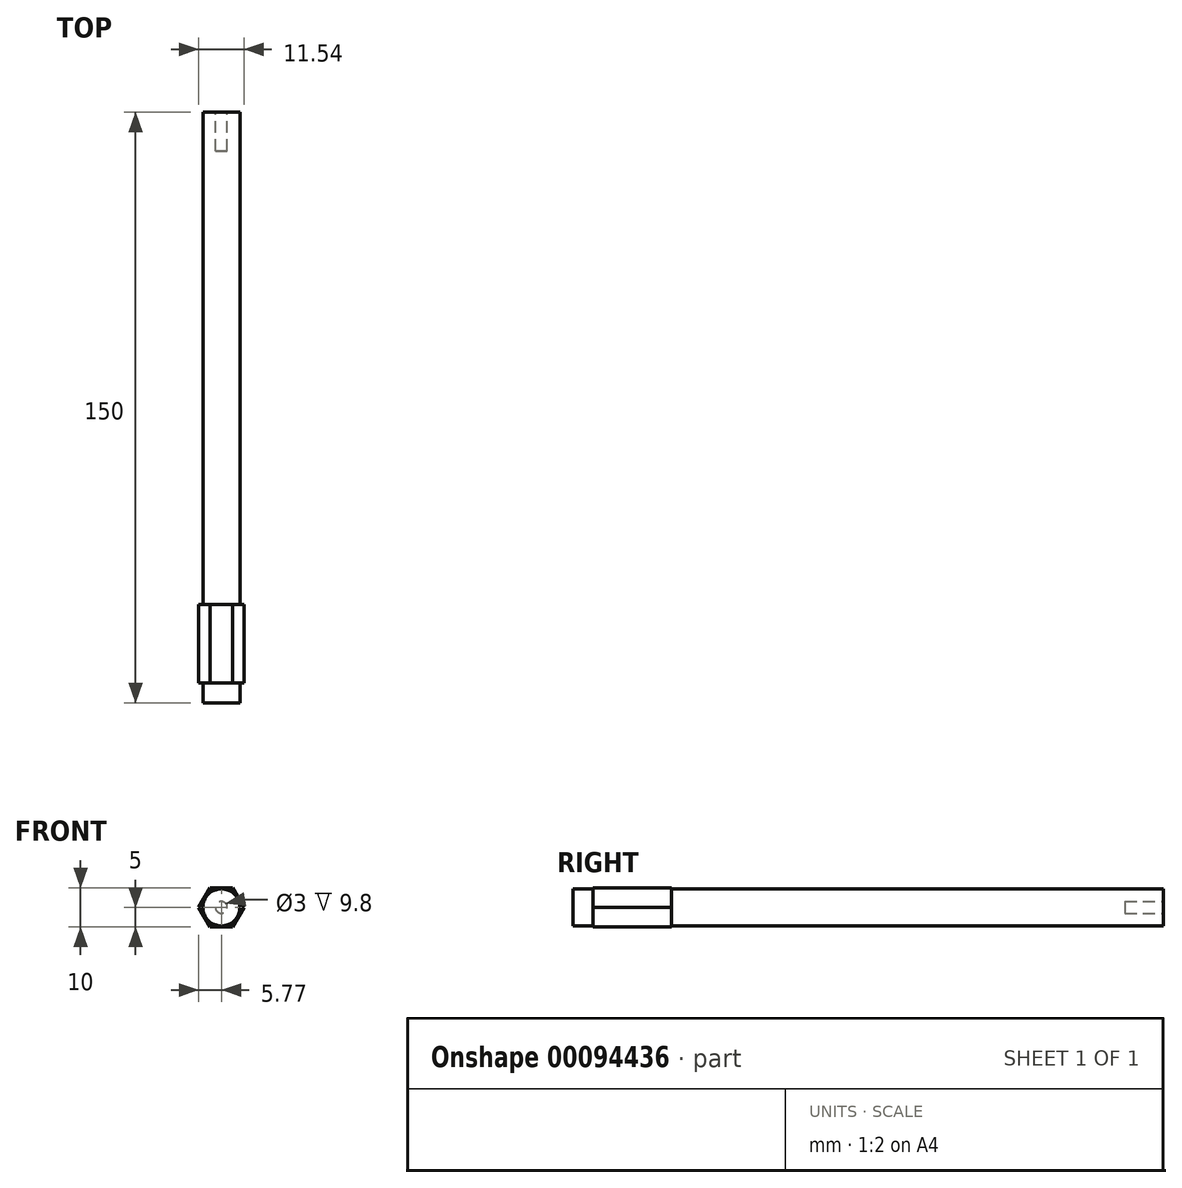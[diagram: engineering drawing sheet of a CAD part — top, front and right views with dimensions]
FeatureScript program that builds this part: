
annotation { "Feature Type Name" : "Feature", "Feature Type Description" : "" }
export const myFeature = defineFeature(function(context is Context, id is Id, definition is map)
    precondition{}
    {
        {
            var Q0;
            Q0=qCreatedBy(makeId("Front.planeOp"),FACE);
            var sketch = newSketch(context, id + "F0", { "sketchPlane" : qUnion([Q0])});
            skCircle(sketch, "E0", {"center": v(0, 0) * mm, "radius": 4.7 * mm});
            skSolve(sketch);
        }
        {
            var Q0;
            Q0 = qSketchRegion(id + "F0", true);
            extrude(context, id + "F1", {"entities" : qUnion([Q0]), "depth" : 150 * mm});
        }
        {
            var Q0;
            Q0=makeQuery(id+"F1.opExtrude","CAP_FACE",FACE,{"disambiguationData":[OSD([sQuery(id+"F0.wireOp",EDGE,"E0")])],"isStart":true});
            var sketch = newSketch(context, id + "F2", { "sketchPlane" : qUnion([Q0])});
            skCircle(sketch, "E1", {"center": v(0, 0) * mm, "radius": 1.5 * mm});
            skSolve(sketch);
        }
        {
            var Q0;
            Q0 = qSketchRegion(id + "F2", true);
            extrude(context, id + "F3", {"entities" : qUnion([Q0]), "operationType" : NewBodyOperationType.REMOVE, "oppositeDirection" : true, "depth" : 9.8 * mm});
        }
        {
            var Q0;
            Q0=makeQuery(id+"F1.opExtrude","CAP_FACE",FACE,{"disambiguationData":[OSD([sQuery(id+"F0.wireOp",EDGE,"E0")])],"isStart":false});
            cPlane(context, id + "F4", {"entities" : qUnion([Q0]), "cplaneType" : CPlaneType.OFFSET, "offset" : 5 * mm, "oppositeDirection" : true, "width" : 150 * mm, "height" : 150 * mm});
        }
        {
            var Q0;
            Q0=qCreatedBy(id+"F4.planeOp",FACE);
            var sketch = newSketch(context, id + "F5", { "sketchPlane" : qUnion([Q0])});
            skCircle(sketch, "E2.cCircle", {"center": v(0, 0) * mm, "radius": 5 * mm, "construction": true});
            skLineSegment(sketch, "E2.0", {"start": v(-2.89, 5) * mm, "end": v(2.89, 5) * mm});
            skLineSegment(sketch, "E2.1", {"start": v(2.89, 5) * mm, "end": v(5.77, 0) * mm});
            skLineSegment(sketch, "E2.2", {"start": v(5.77, 0) * mm, "end": v(2.89, -5) * mm});
            skLineSegment(sketch, "E2.3", {"start": v(2.89, -5) * mm, "end": v(-2.89, -5) * mm});
            skLineSegment(sketch, "E2.4", {"start": v(-2.89, -5) * mm, "end": v(-5.77, 0) * mm});
            skLineSegment(sketch, "E2.5", {"start": v(-5.77, 0) * mm, "end": v(-2.89, 5) * mm});
            skPoint(sketch, "E2.0.midPoint", {"position": v(0, 5) * mm});
            skSolve(sketch);
        }
        {
            var Q0;
            Q0 = qSketchRegion(id + "F5", true);
            extrude(context, id + "F6", {"entities" : qUnion([Q0]), "operationType" : NewBodyOperationType.ADD, "oppositeDirection" : true, "depth" : 20 * mm});
        }
    });
